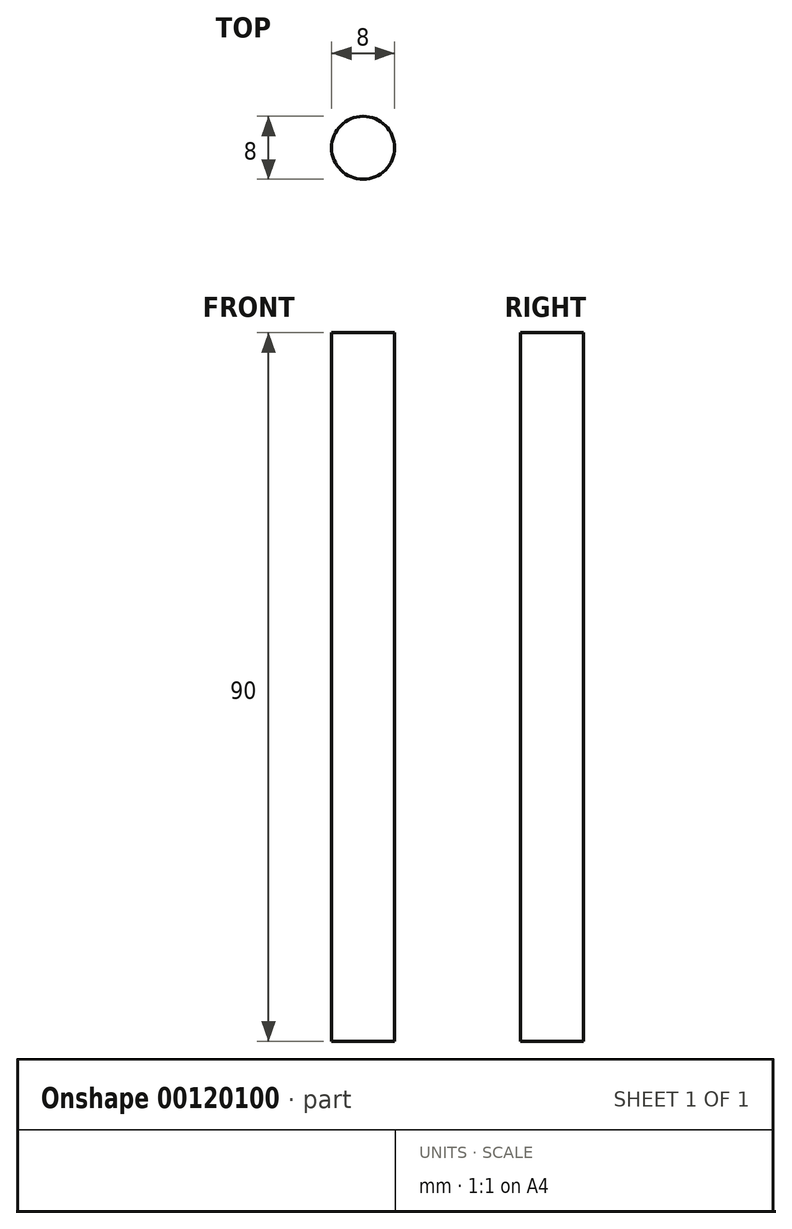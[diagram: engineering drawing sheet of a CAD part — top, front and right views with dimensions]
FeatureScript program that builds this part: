
annotation { "Feature Type Name" : "Feature", "Feature Type Description" : "" }
export const myFeature = defineFeature(function(context is Context, id is Id, definition is map)
    precondition{}
    {
        {
            var Q0;
            Q0=qCreatedBy(makeId("Top.planeOp"),FACE);
            var sketch = newSketch(context, id + "F0", { "sketchPlane" : qUnion([Q0])});
            skCircle(sketch, "E0", {"center": v(0, 0) * mm, "radius": 4 * mm});
            skSolve(sketch);
        }
        {
            var Q0;
            Q0 = qSketchRegion(id + "F0", true);
            extrude(context, id + "F1", {"entities" : qUnion([Q0]), "endBound" : BoundingType.SYMMETRIC, "depth" : 90 * mm});
        }
    });
